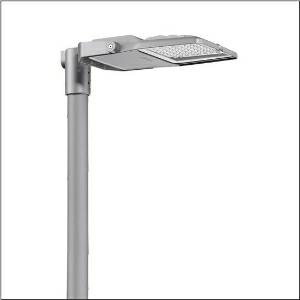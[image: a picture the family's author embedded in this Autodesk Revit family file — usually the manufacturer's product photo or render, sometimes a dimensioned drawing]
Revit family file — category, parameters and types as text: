
# Revit family: floodlight_fl_21_mini___pl64_5xa7775d2e3a_010e
name_source: partatom
category: Lighting Fixtures
units: mm (PartAtom-declared; Revit-internal decimal feet)

## family parameters
Cut with Voids When Loaded = No
Host = Face
Light Source = No
Part Type = Normal
Room Calculation Point = No
Round Connector Dimension = Use Diameter
Shared = No

## types (1)
- --- (1 x LED, 17220 lm, 142.9 W, 3000K)
    Apparent Load = 143 VA
    CIE Flux Codes = 28 80 98 100 100
    Color Rendering = 70
    Color Temperature = 3000K
    Default Elevation = 1800 mm
    Description = Floodlight FL 21 mini, floodlight, primary light control with lens, of PMMA, primary optical cover: protective disc, of toughened safety glass, transparent, light distribution: PL64, light emission: direct distribution, installation type: surface-mounted, LED, High Power LED, rated luminous flux: 17.220lm, luminous efficacy: 121lm/W, light colour: 730, colour temperature: 3000K, control gear: Smart Interface (Zhaga), control: flexible luminous flux parameterisation, time-dependent luminous flux control, constant luminous flux control, overheat protection, pre-setting: logarithmic dimming characteristic, with terminal, 6-pole, mains connection: 220..240V, AC, 50/60Hz, start of lifetime: 143W, end of service life: 151W, reduction: 63W, luminaire housing, of diecast aluminium, powder-coated, Siteco® metallic grey (DB 702S), corrosivity category C5 mid according to DIN EN ISO 12944, suitable for swimming pools, chlorine-resistant, sealing non-destructively replaceable, please order mast flange separately, mast bracket, of steel, galvanised, powder-coated, Siteco® metallic grey (DB 702S), Smart Interface above, protection rating (complete): IP66, insulation class (complete): insulation class II (safety insulation), certification: CE, ENEC, VDE, protection symbol: D, impact resistance: IK08, permissible operating ambient temperature: -40..+40°C, permissible operating ambient temperature for outdoor applications: -40..+50°C, standard: DIN EN 12944, LABS conformity tested according to VDMA 24364:2018-05, packaging unit: 1 piece

Light Distribution: PL64
    Height = 70 mm
    Lamp = 1 x LED
    Lamp Light Flux = 17220 lm
    Lamp Power = 142.9 W
    Lamp count = 1
    Length = 485 mm
    Luminous efficacy = 121 lm/W
    Manufacturer = Siteco
    ModVariant = No
    Model = 5XA7775D2E3A
    Number of Poles = 1
    OnlyDefault = Yes
    Power Factor = 1
    Product Name = Floodlight FL 21 mini | PL64
    Product group = floodlight | pylon annexe
    ProductGroupID = 6201
    Protection Class = Protection class II
    Protection Degree = IP 66
    RLX_Detail_Level = 1
    RLX_Emergency_Light_Flux = 0 lm
    RLX_Emergency_Type = 0
    RLX_Emergency_Type_DB = No
    RlxData = <blob elided: 101369 chars, md5=82563b30>
    Socket = socket
    Standby Power = 0 W
    System Light Flux = 17220 lm
    System Power = 143 W
    Type Comments = factory setting: luminous flux: 100 % | dim-lin: 254 | 730 mA
    Type Image = l_1007125.jpg
    URL = http://relux.com
    VarID = @adj_186733
    Voltage = 0 V
    Weight = 0.00 kg
    Width = 337 mm

## geometry (parser evidence)
native form markers: Blend x4, Sweep x12
no freeform markers — native parametric forms only
